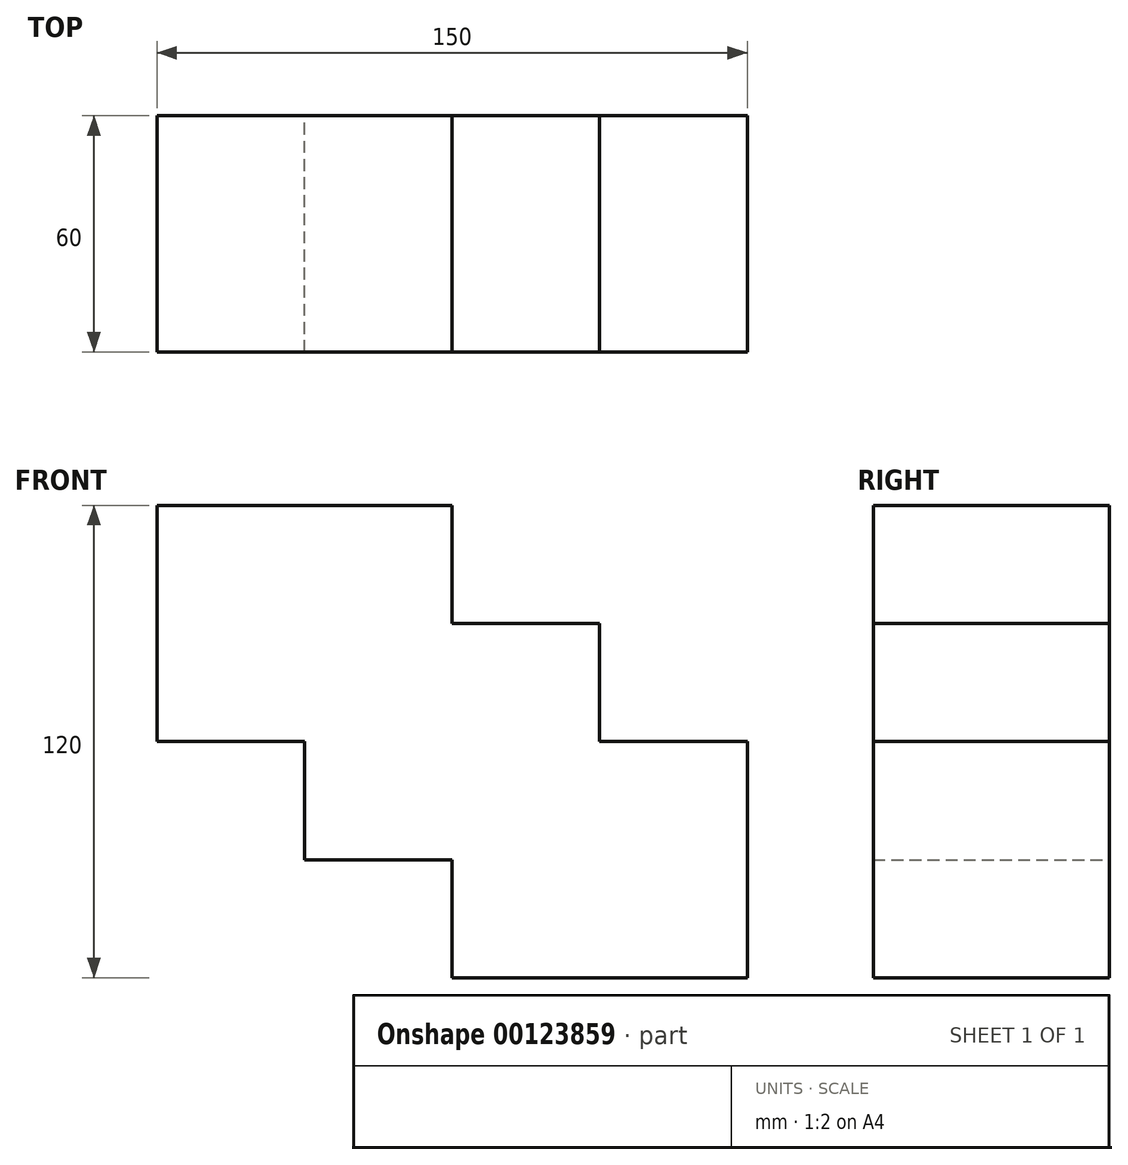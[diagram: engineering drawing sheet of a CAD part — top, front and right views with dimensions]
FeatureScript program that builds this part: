
annotation { "Feature Type Name" : "Feature", "Feature Type Description" : "" }
export const myFeature = defineFeature(function(context is Context, id is Id, definition is map)
    precondition{}
    {
        {
            var Q0;
            Q0=qCreatedBy(makeId("Front.planeOp"),FACE);
            var sketch = newSketch(context, id + "F0", { "sketchPlane" : qUnion([Q0])});
            skLineSegment(sketch, "E0.bottom", {"start": v(0, 0) * mm, "end": v(-75, 0) * mm});
            skLineSegment(sketch, "E0.top", {"start": v(0, 60) * mm, "end": v(-75, 60) * mm});
            skLineSegment(sketch, "E0.left", {"start": v(0, 0) * mm, "end": v(0, 60) * mm});
            skLineSegment(sketch, "E0.right", {"start": v(-75, 0) * mm, "end": v(-75, 60) * mm});
            skLineSegment(sketch, "E1.bottom", {"start": v(0, 0) * mm, "end": v(75, 0) * mm});
            skLineSegment(sketch, "E1.top", {"start": v(0, -60) * mm, "end": v(75, -60) * mm});
            skLineSegment(sketch, "E1.left", {"start": v(0, 0) * mm, "end": v(0, -60) * mm});
            skLineSegment(sketch, "E1.right", {"start": v(75, 0) * mm, "end": v(75, -60) * mm});
            skLineSegment(sketch, "E2.bottom", {"start": v(37.5, 30) * mm, "end": v(-37.5, 30) * mm});
            skLineSegment(sketch, "E2.top", {"start": v(37.5, -30) * mm, "end": v(-37.5, -30) * mm});
            skLineSegment(sketch, "E2.left", {"start": v(37.5, 30) * mm, "end": v(37.5, -30) * mm});
            skLineSegment(sketch, "E2.right", {"start": v(-37.5, 30) * mm, "end": v(-37.5, -30) * mm});
            skPoint(sketch, "E2.middle", {"position": v(0, 0) * mm});
            skSolve(sketch);
        }
        {
            var Q0;
            Q0 = qSketchRegion(id + "F0", true);
            extrude(context, id + "F1", {"entities" : qUnion([Q0]), "depth" : 60 * mm});
        }
    });
